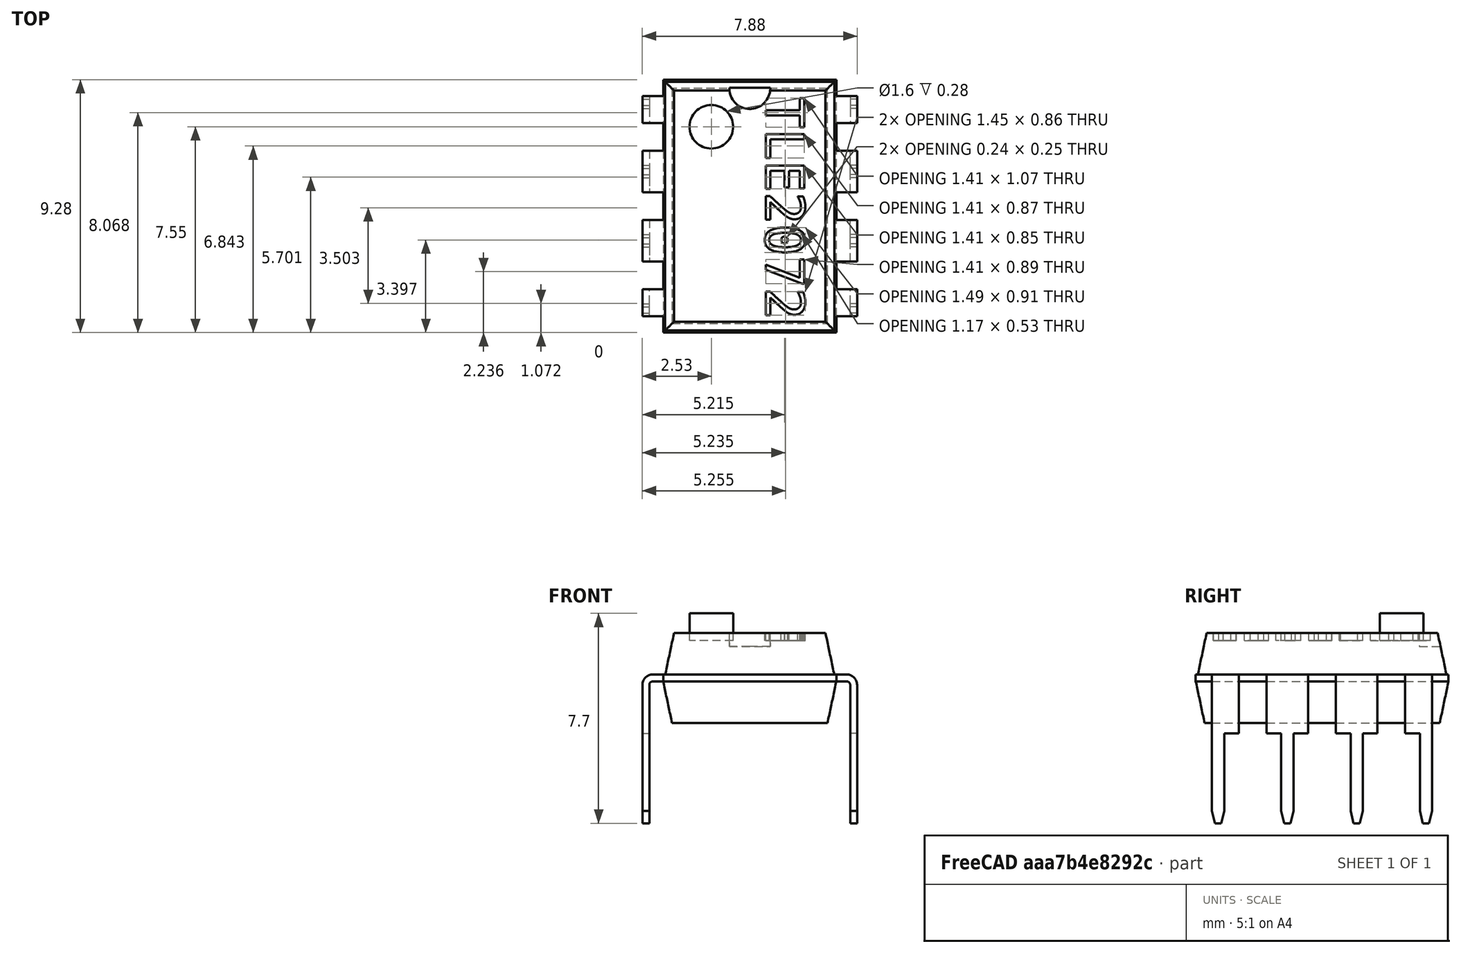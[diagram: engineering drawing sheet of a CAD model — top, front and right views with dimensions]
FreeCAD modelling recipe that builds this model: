
FCSTD DOCUMENT  (FreeCAD 0.18.4R)
Label: TLE2072ACP
License: All rights reserved
LicenseURL: http://en.wikipedia.org/wiki/All_rights_reserved
objects: Part::Feature×2, Part::Part2DObjectPython×1, Part::Extrusion×1, Part::Cylinder×1, Part::Cut×1
note: 6 computed .brp shape members not serialized (recipe doc carries the construction recipe); baked Part::Feature solids carry a one-line shape summary decoded from their .brp

FEATURE [Part::Feature] Part__Feature  label="DIP-8_W7.62mm"
  shape: bbox 7.874 x 9.27 x 6.98 mm, 148 faces (baked)
FEATURE [Part::Part2DObjectPython] ShapeString  # Draft 2D object (typed FeaturePython)
  FontFile = <path>
  Size = 1.5
  String = TLE2072
  Support = -> [Part__Feature]
  Tracking = 0
FEATURE [Part::Extrusion] Extrude
  Base = -> ShapeString
  Dir = (0,0,1)
  DirMode = 2
  FaceMakerClass = Part::FaceMakerBullseye
  LengthFwd = 1
  LengthRev = 0
  Placement = pos=(4.4,0.2,3.4) rot=(0,0,1;4.71239rad)
  Solid = true
  Symmetric = false
FEATURE [Part::Cylinder] Cylinder
  Angle = 360
  AttacherType = Attacher::AttachEngine3D
  Height = 1
  Placement = pos=(2.4,-0.9,3.4) rot=(0,0,1;0rad)
  Radius = 0.8
FEATURE [Part::Cut] Cut  label="TLE2072"
  Base = -> Part__Feature
  Tool = -> Extrude
FEATURE [Part::Feature] Shape  label="TLE2073"
  shape: bbox 7.874 x 9.27 x 6.98 mm, 258 faces (baked)
note: 1 file-system path scrubbed to <path> (originals preserved in the JSON sidecar)
